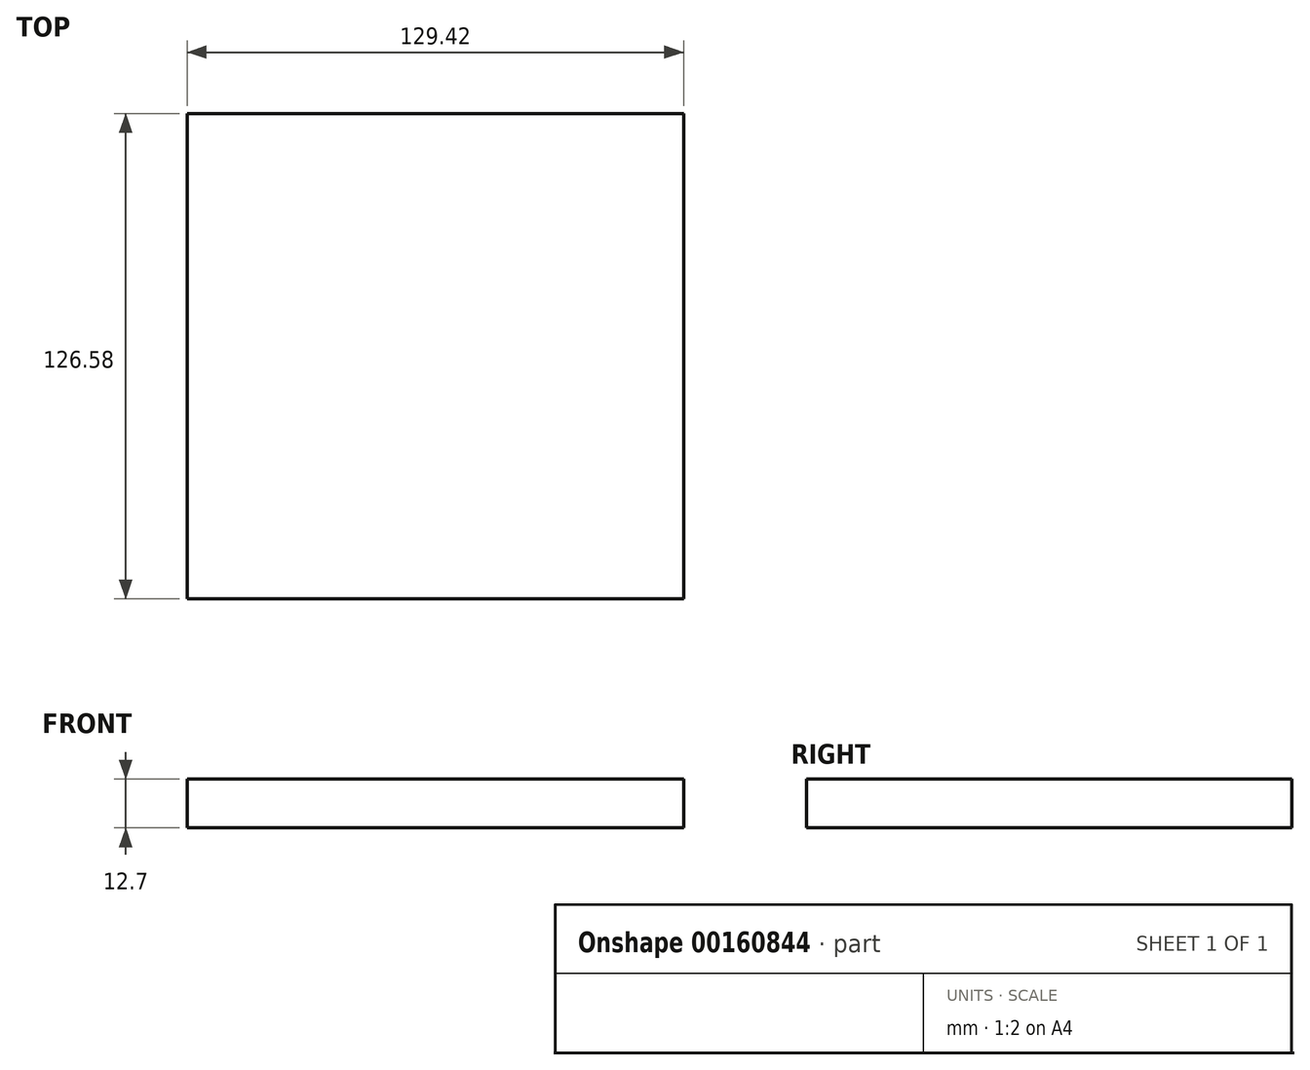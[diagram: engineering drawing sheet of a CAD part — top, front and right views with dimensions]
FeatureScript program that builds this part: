
annotation { "Feature Type Name" : "Feature", "Feature Type Description" : "" }
export const myFeature = defineFeature(function(context is Context, id is Id, definition is map)
    precondition{}
    {
        {
            var Q0;
            Q0=qCreatedBy(makeId("Top.planeOp"),FACE);
            var sketch = newSketch(context, id + "F0", { "sketchPlane" : qUnion([Q0])});
            skLineSegment(sketch, "E0.bottom", {"start": v(64.71, 63.29) * mm, "end": v(-64.71, 63.29) * mm});
            skLineSegment(sketch, "E0.top", {"start": v(64.71, -63.29) * mm, "end": v(-64.71, -63.29) * mm});
            skLineSegment(sketch, "E0.left", {"start": v(64.71, 63.29) * mm, "end": v(64.71, -63.29) * mm});
            skLineSegment(sketch, "E0.right", {"start": v(-64.71, 63.29) * mm, "end": v(-64.71, -63.29) * mm});
            skPoint(sketch, "E0.middle", {"position": v(0, 0) * mm});
            skSolve(sketch);
        }
        {
            var Q0;
            Q0=makeQuery(id+"F0.imprint","IMPRINT",FACE,{"disambiguationData":[TD([[makeQuery(id+"F0.imprint","IMPRINT",EDGE,{"derivedFrom":sQuery(id+"F0.wireOp",EDGE,"E0.bottom")}),1.0]])]});
            extrude(context, id + "F1", {"entities" : qUnion([Q0]), "depth" : 12.7 * mm});
        }
    });
